# Revit family: Воздухоотводчик автоматический Airvent
name_source: partatom
category: Арматура трубопроводов
revit_build: Autodesk Revit 2017 (Build: 20190508_0315(x64)
units: mm (PartAtom-declared; Revit-internal decimal feet)

## family parameters
Всегда вертикально = Да
На основе рабочей плоскости = Нет
Общий = Нет
При загрузке вырезать с полостями = Нет
Размер круглого соединителя = Использовать диаметр
Тип детали = Присоединяется

## types (2) — shared parameters
ADSK_Версия Revit = 2017
ADSK_Версия семейства = v1
ADSK_Единица измерения = шт.
ADSK_Завод-изготовитель = Danfoss
ADSK_Количество = 1
ADSK_Марка = Airvent
ADSK_Обозначение = Airvent
D = 45 мм
H = 70 мм
H_УГО = 60 мм
PN = 10
Tmax = 110 °C
Tmin = 0 °C
URL = https://www.danfoss.com
Допустимые среды = Вода или 40 % водный раствор гликоля
Изготовитель = Danfoss
Изготовитель (телефон) = +7(495)792-57-57
Материал_Корпус = Danfoss Латунь
Разработчик = ООО ПРОРУБИМ
Разработчик (URL) = http://prorubim.com
Разработчик (телефон) = +7(495)649-85-43
Тип присоединения = Наружная резьба

## per-type parameters (varying)
| type | ADSK_Код изделия | ADSK_Масса | ADSK_Масса_Текст | ADSK_Наименование | ADSK_Наименование краткое | ADSK_Размер_Диаметр | Es | Размер присоединения |
| DN10 | 065B8222 | 0.15 | 0.15 | Воздухоотводчик автоматический Airvent, муфтовый, материал корпуса - латунь, DN10, PN10, Тмакс. = 110 °С | Airvent DN10 | 10 мм | 23 мм | G3/8 |
| DN15 | 065B822300 | 0.154 | 0.154 | Воздухоотводчик автоматический Airvent, муфтовый, материал корпуса - латунь, DN15, PN10, Тмакс. = 110 °С | Airvent DN15 | 15 мм | 27 мм | G1/2 |
